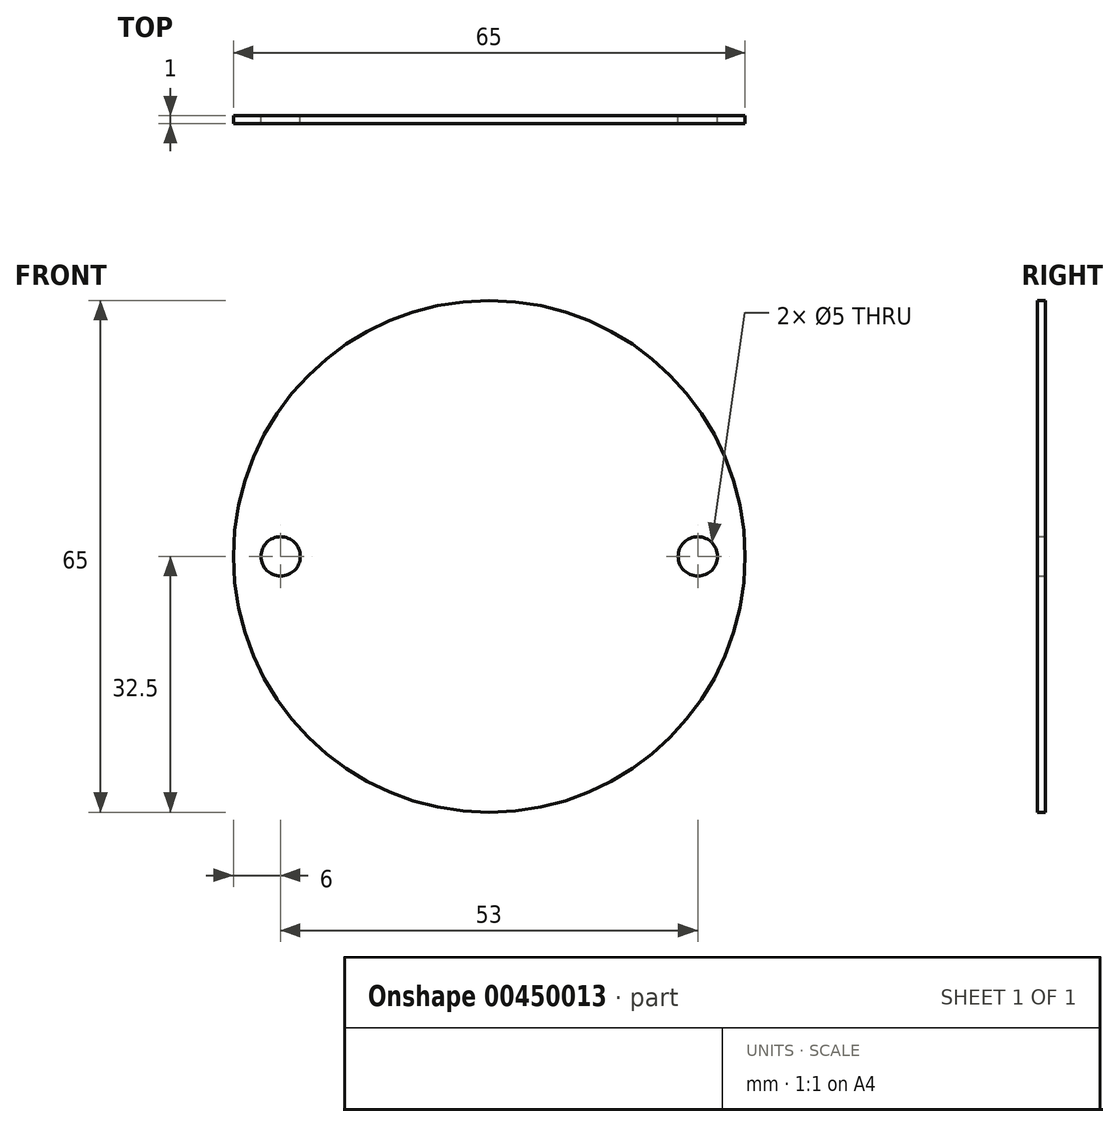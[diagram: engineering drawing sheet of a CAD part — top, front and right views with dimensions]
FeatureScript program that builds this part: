
annotation { "Feature Type Name" : "Feature", "Feature Type Description" : "" }
export const myFeature = defineFeature(function(context is Context, id is Id, definition is map)
    precondition{}
    {
        {
            var Q0;
            Q0=qCreatedBy(makeId("Front.planeOp"),FACE);
            var sketch = newSketch(context, id + "F0", { "sketchPlane" : qUnion([Q0])});
            skCircle(sketch, "E0", {"center": v(0, 0) * mm, "radius": 32.5 * mm});
            skLineSegment(sketch, "E1", {"start": v(0, 0) * mm, "end": v(26.5, 0) * mm, "construction": true});
            skCircle(sketch, "E2", {"center": v(26.5, 0) * mm, "radius": 2.5 * mm});
            skLineSegment(sketch, "E3", {"start": v(0, 32.5) * mm, "end": v(0, -32.5) * mm, "construction": true});
            skCircle(sketch, "E4.MirrorC", {"center": v(-26.5, 0) * mm, "radius": 2.5 * mm});
            skSolve(sketch);
        }
        {
            var Q0;
            Q0 = qSketchRegion(id + "F0", true);
            extrude(context, id + "F1", {"entities" : qUnion([Q0]), "depth" : 1 * mm, "offsetDistance" : 25 * mm});
        }
    });
